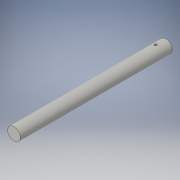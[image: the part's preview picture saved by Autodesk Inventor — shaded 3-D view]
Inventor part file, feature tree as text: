
AUTODESK INVENTOR PART (.ipt)
format: ipt  version: 2016 (Build 200138000, 138)  size: 94,720 bytes
history: native  units: in
note: dims shown in document units (in); Inventor stores cm internally (conversion verified against a paired STEP export)
features: extrude x2, sketch x2
ambient origin geometry x8: Origin, YZ Plane, XZ Plane, XY Plane, X Axis, Y Axis, Z Axis, Center Point
bodies: Solid1 (feature_tree)
feature tree (4):
  extrude  "Extrusion1"  Depth=12.0in TaperAngle=0.0deg
  extrude  "Extrusion3"  Depth=12.0in TaperAngle=0.0deg
  sketch  "Sketch1"  dims[d0=1.0in d1=12.0in d2=0.0in]
  sketch  "Sketch3"  dims[d6=0.2in d7=12.0in d8=0.0in]
